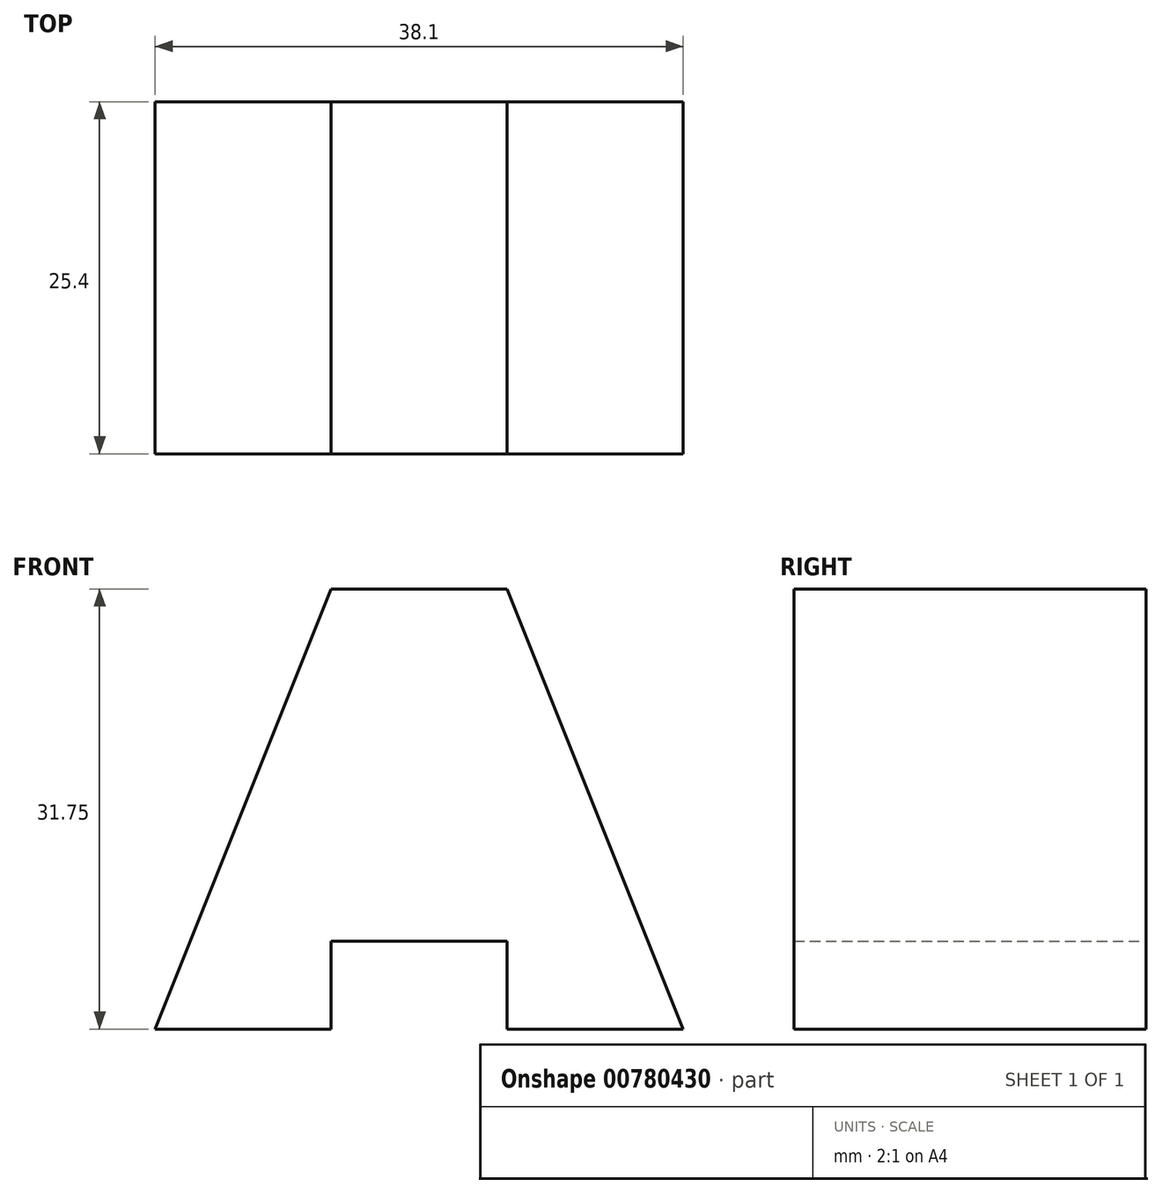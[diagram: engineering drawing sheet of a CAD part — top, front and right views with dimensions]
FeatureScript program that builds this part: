
annotation { "Feature Type Name" : "Feature", "Feature Type Description" : "" }
export const myFeature = defineFeature(function(context is Context, id is Id, definition is map)
    precondition{}
    {
        {
            var Q0;
            Q0=qCreatedBy(makeId("Front.planeOp"),FACE);
            var sketch = newSketch(context, id + "F0", { "sketchPlane" : qUnion([Q0])});
            skLineSegment(sketch, "E0", {"start": v(0, 0) * mm, "end": v(12.7, 0) * mm});
            skLineSegment(sketch, "E1", {"start": v(12.7, 0) * mm, "end": v(12.7, 6.35) * mm});
            skLineSegment(sketch, "E2", {"start": v(12.7, 6.35) * mm, "end": v(25.4, 6.35) * mm});
            skLineSegment(sketch, "E3", {"start": v(25.4, 6.35) * mm, "end": v(25.4, 0) * mm});
            skLineSegment(sketch, "E4", {"start": v(25.4, 0) * mm, "end": v(38.1, 0) * mm});
            skLineSegment(sketch, "E5", {"start": v(12.7, 31.75) * mm, "end": v(25.4, 31.75) * mm});
            skLineSegment(sketch, "E6", {"start": v(25.4, 31.75) * mm, "end": v(38.1, 0) * mm});
            skLineSegment(sketch, "E7", {"start": v(12.7, 31.75) * mm, "end": v(0, 0) * mm});
            skSolve(sketch);
        }
        {
            var Q0;
            Q0 = qSketchRegion(id + "F0", true);
            extrude(context, id + "F1", {"entities" : qUnion([Q0]), "depth" : 25.4 * mm, "offsetDistance" : 25.4 * mm});
        }
    });
